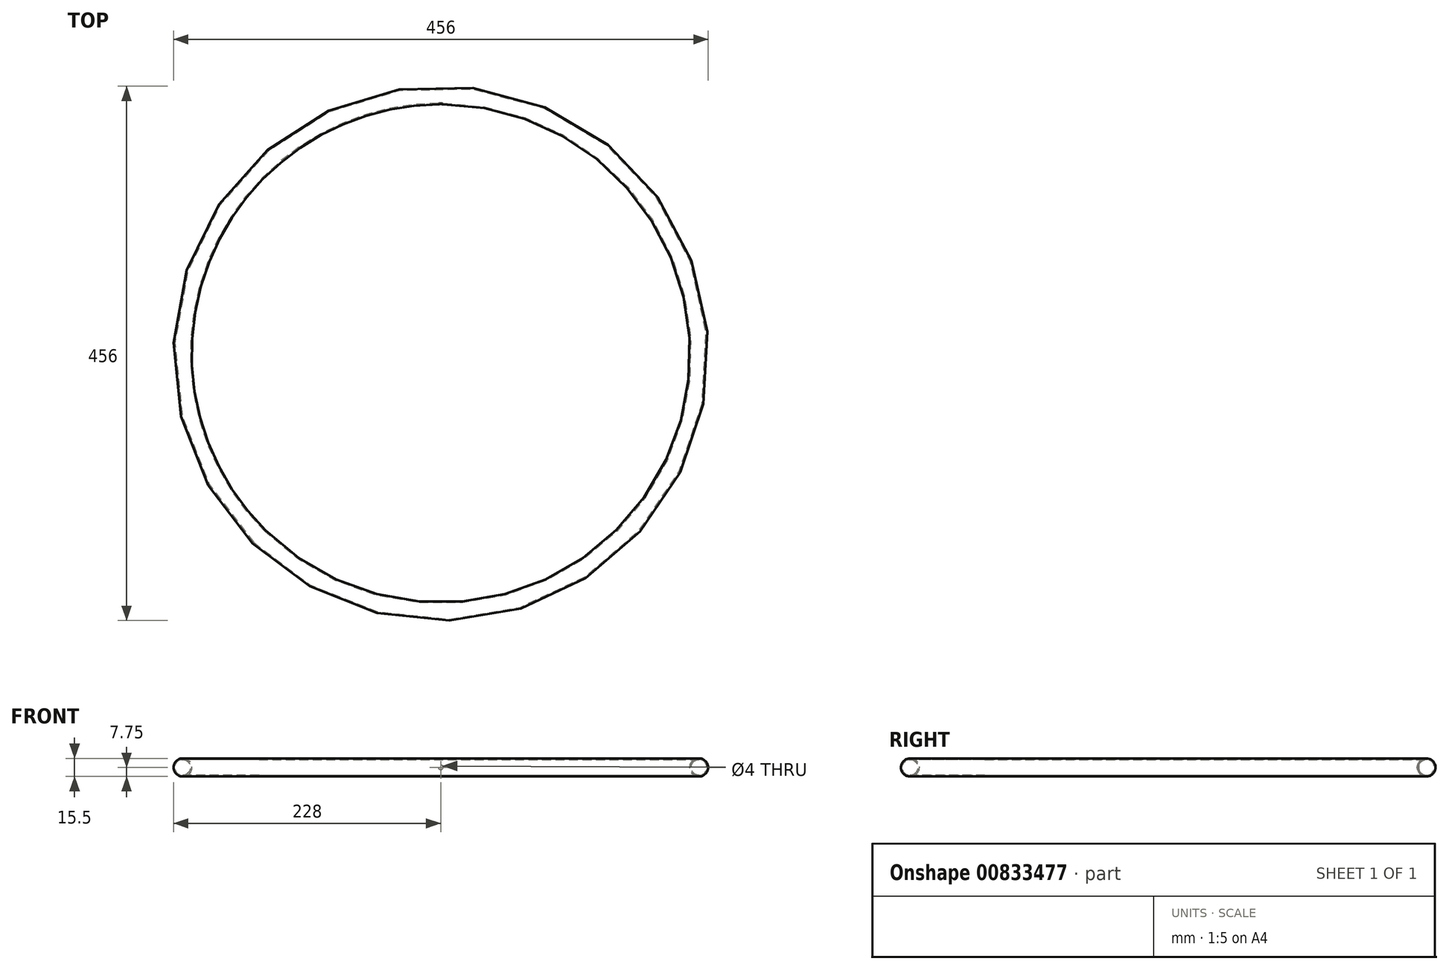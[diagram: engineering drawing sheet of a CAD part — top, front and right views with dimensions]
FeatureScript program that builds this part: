
annotation { "Feature Type Name" : "Feature", "Feature Type Description" : "" }
export const myFeature = defineFeature(function(context is Context, id is Id, definition is map)
    precondition{}
    {
        {
            var Q0;
            Q0=qCreatedBy(makeId("Front.planeOp"),FACE);
            var sketch = newSketch(context, id + "F0", { "sketchPlane" : qUnion([Q0])});
            skLineSegment(sketch, "E0", {"start": v(0, 32.7) * mm, "end": v(0, -27.4) * mm, "construction": true});
            skCircle(sketch, "E1", {"center": v(220.25, 0) * mm, "radius": 7.75 * mm});
            skCircle(sketch, "E2", {"center": v(220.25, 0) * mm, "radius": 6.75 * mm});
            skSolve(sketch);
        }
        {
            var Q0;
            Q0=makeQuery(id+"F0.imprint","IMPRINT",FACE,{"disambiguationData":[TD([[makeQuery(id+"F0.imprint","IMPRINT",EDGE,{"derivedFrom":sQuery(id+"F0.wireOp",EDGE,"E1")}),1.0]])]});
            var Q1;
            Q1=sQuery(id+"F0.wireOp",EDGE,"E0");
            revolve(context, id + "F1", {"surfaceOperationType" : NewSurfaceOperationType.NEW, "entities" : qUnion([Q0]), "axis" : qUnion([Q1]), "revolveType" : RevolveType.FULL});
        }
        {
            var Q0;
            Q0=qCreatedBy(makeId("Front.planeOp"),FACE);
            var sketch = newSketch(context, id + "F2", { "sketchPlane" : qUnion([Q0])});
            skPoint(sketch, "E3", {"position": v(0, 0) * mm});
            skLineSegment(sketch, "E4", {"start": v(0, 0) * mm, "end": v(0, 122.23) * mm});
            skSolve(sketch);
        }
        {
            var Q0;
            Q0=sQuery(id+"F2.wireOp",VERTEX,"E3");
            var Q1;
            Q1=makeQuery(id+"F1.opRevolve","SWEPT_BODY",BODY,{"disambiguationData":[OSD([sQuery(id+"F0.wireOp",EDGE,"E1"),sQuery(id+"F0.wireOp",EDGE,"E2")])]});
            hole(context, id + "F3", {"style" : HoleStyle.SIMPLE, "endStyle" : HoleEndStyle.BLIND, "holeDiameter" : 4 * mm, "majorDiameter" : 5 * mm, "holeDepth" : 12 * mm, "isTappedThrough" : true, "tappedDepth" : 12 * mm, "tapClearance" : 3, "locations" : qUnion([Q0]), "scope" : qUnion([Q1])});
        }
        {
            var Q0;
            Q0=qCreatedBy(makeId("Front.planeOp"),FACE);
            var sketch = newSketch(context, id + "F4", { "sketchPlane" : qUnion([Q0])});
            skLineSegment(sketch, "E5", {"start": v(0, 100.91) * mm, "end": v(0, -110.6) * mm});
            skSolve(sketch);
        }
    });
